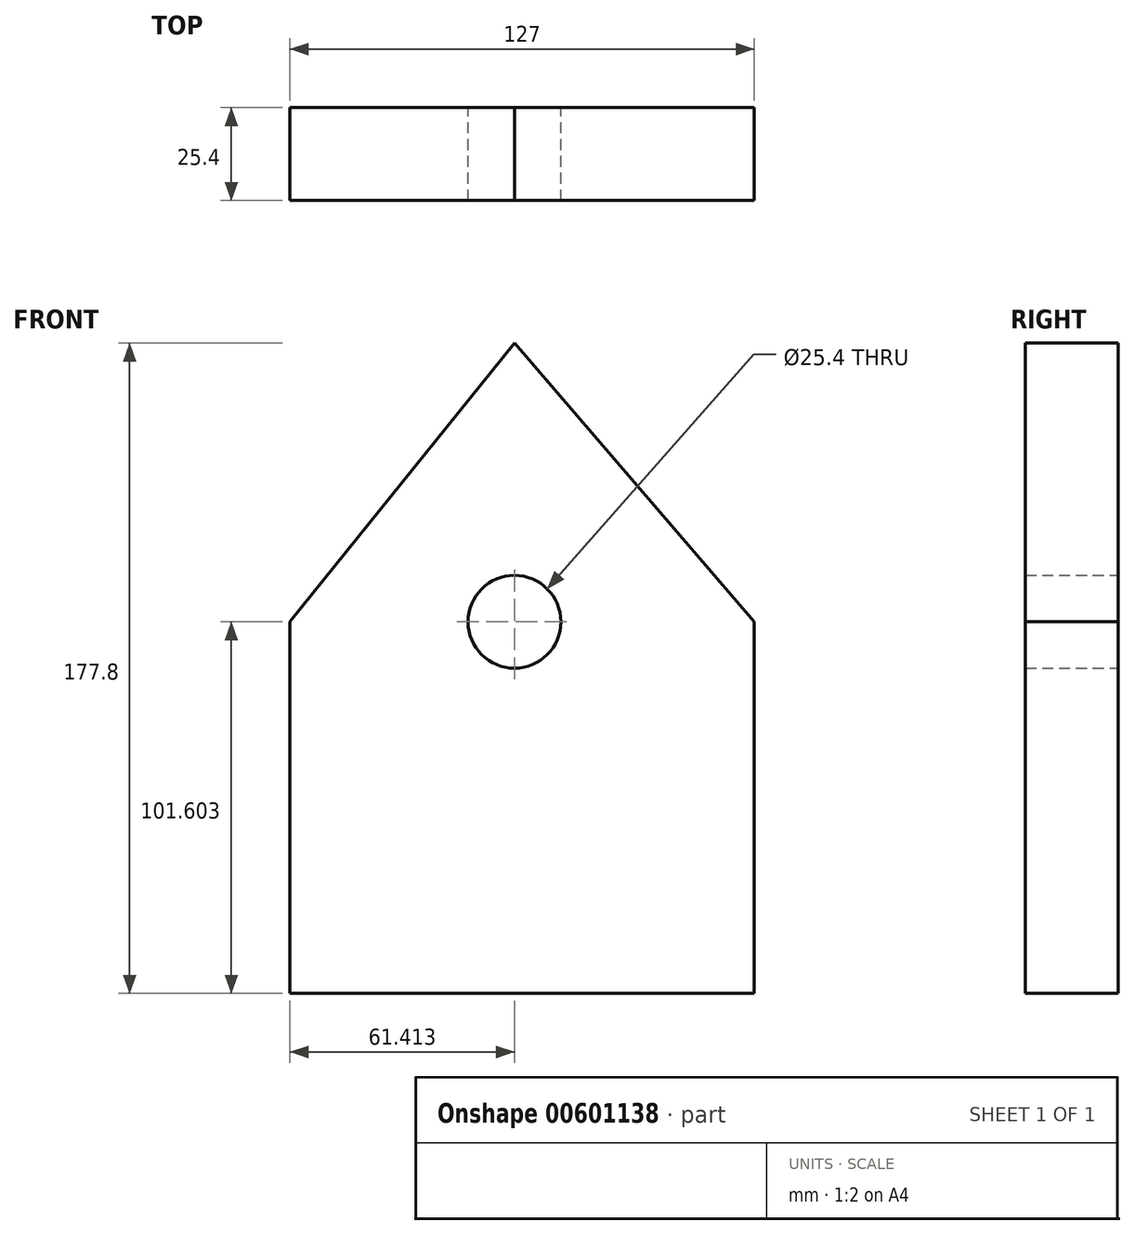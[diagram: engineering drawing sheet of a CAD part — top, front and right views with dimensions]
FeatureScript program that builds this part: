
annotation { "Feature Type Name" : "Feature", "Feature Type Description" : "" }
export const myFeature = defineFeature(function(context is Context, id is Id, definition is map)
    precondition{}
    {
        {
            var Q0;
            Q0=qCreatedBy(makeId("Front.planeOp"),FACE);
            var sketch = newSketch(context, id + "F0", { "sketchPlane" : qUnion([Q0])});
            skLineSegment(sketch, "E0", {"start": v(-66.73, -61.88) * mm, "end": v(-66.73, 39.72) * mm});
            skLineSegment(sketch, "E1", {"start": v(60.27, 39.72) * mm, "end": v(60.27, -61.88) * mm});
            skLineSegment(sketch, "E2", {"start": v(60.27, -61.88) * mm, "end": v(-66.73, -61.88) * mm});
            skLineSegment(sketch, "E3", {"start": v(-66.73, 39.72) * mm, "end": v(-5.32, 115.92) * mm});
            skLineSegment(sketch, "E4", {"start": v(-5.32, 115.92) * mm, "end": v(60.27, 39.72) * mm});
            skPoint(sketch, "E5.endSnap0", {"position": v(-3.23, -61.88) * mm});
            skCircle(sketch, "E6", {"center": v(-5.32, 39.72) * mm, "radius": 12.7 * mm});
            skSolve(sketch);
        }
        {
            var Q0;
            Q0=makeQuery(id+"F0.imprint","IMPRINT",FACE,{"disambiguationData":[TD([[makeQuery(id+"F0.imprint","IMPRINT",EDGE,{"derivedFrom":sQuery(id+"F0.wireOp",EDGE,"E0")}),-1.0]])]});
            extrude(context, id + "F1", {"entities" : qUnion([Q0]), "depth" : 25.4 * mm, "offsetDistance" : 25.4 * mm});
        }
    });
